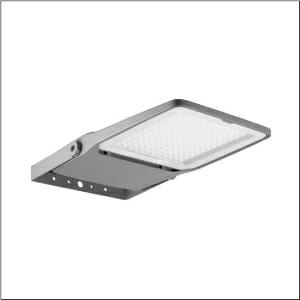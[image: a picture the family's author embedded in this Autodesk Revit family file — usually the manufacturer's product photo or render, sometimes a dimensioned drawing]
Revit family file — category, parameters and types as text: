
# Revit family: floodlight_fl_20_midi___pl43_5xa7682e3a2ac_3a80
name_source: partatom
category: Lighting Fixtures
units: mm (PartAtom-declared; Revit-internal decimal feet)

## family parameters
Cut with Voids When Loaded = No
Host = Face
Light Source = No
Part Type = Normal
Room Calculation Point = No
Round Connector Dimension = Use Diameter
Shared = No

## types (1)
- --- (1 x LED 5000K / CRI = 70 (unbekannt), 28900 lm, 5000K)
    Apparent Load = 208 VA
    CIE Flux Codes = 32 74 99 100 100
    Color Rendering = 70
    Color Temperature = 5000K
    Default Elevation = 1800 mm
    Description = Floodlight FL 20 midi, floodlight, primary light control with lens, of plastic, primary optical cover: protective disc, of toughened safety glass, transparent, light distribution: PL43, light emission: direct distribution, primary light characteristic: asymmetric, installation type: surface-mounted, LED, High Power LED, rated luminous flux: 28.900lm, luminous efficacy: 139lm/W, light colour: 750, colour temperature: 5000K, control gear: ECG Plus, control: flexible luminous flux parameterisation, time-dependent luminous flux control, digital communication interface, power reduction, overheat protection, electronic power reduction, with terminal, 5-pole, max. 2.5mm², mains connection: 220..240V, AC, 50/60Hz, rated input power: 208W, LED unit, of diecast aluminium, powder-coated, Siteco® metallic grey (DB 702S), corrosivity category C5 mid according to DIN EN ISO 12944, incl. 1x M20 cable gland for cable Ø 6.5..12mm, length: 731mm, width: 450mm, height: 76mm, housing frame, of diecast aluminium, powder-coated, Siteco® metallic grey (DB 702S), wall fastening, of steel, powder-coated, Siteco® metallic grey (DB 702S), DALI, protection rating (complete): IP66, insulation class (complete): insulation class II (safety insulation), certification: CE, ENEC, VDE, protection symbol: D, permissible operating ambient temperature: -40..+40°C, permissible operating ambient temperature for outdoor applications: -40..+50°C, standard: DIN EN 12944, packaging unit: 1 piece

Light Distribution: PL43
    Height = 76 mm
    Lamp = 1 x LED 5000K / CRI >= 70 (unbekannt)
    Lamp Light Flux = 28900 lm
    Lamp count = 1
    Length = 731 mm
    Luminous efficacy = 139 lm/W
    Manufacturer = Siteco
    ModVariant = No
    Model = 5XA7682E3A2AC
    Mounting Place = Wall
    Mounting Type = Surface mounted
    Number of Poles = 1
    OnlyDefault = Yes
    Power Factor = 1
    Product Name = Floodlight FL 20 midi | PL43
    Product group = floodlight | wall mounted
    ProductGroupID = 2001
    Protection Class = Protection class II
    Protection Degree = IP 66
    RLX_Detail_Level = 1
    RLX_Emergency_Light_Flux = 0 lm
    RLX_Emergency_Type = 0
    RLX_Emergency_Type_DB = No
    RlxData = <blob elided: 92189 chars, md5=18ab02ce>
    Socket = socket
    Standby Power = 0 W
    System Light Flux = 28900 lm
    System Power = 208 W
    Type Comments = factory setting: luminous flux: 100 % | dim-lin: 254 | 484 mA
    Type Image = l_1005944.jpg
    URL = http://relux.com
    VarID = @adj_148185
    Voltage = 0 V
    Weight = 0.00 kg
    Width = 450 mm

## geometry (parser evidence)
native form markers: Blend x4, Sweep x12
no freeform markers — native parametric forms only
